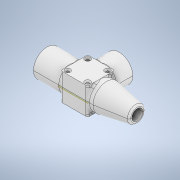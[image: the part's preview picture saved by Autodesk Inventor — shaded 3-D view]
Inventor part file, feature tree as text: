
AUTODESK INVENTOR PART (.ipt)
format: ipt  version: 2020 (Build 240168000, 168)  size: 861,696 bytes
history: native  units: mm
features: sketch x9, extrude x8, fillet x5, move_body x3, plane x2, chamfer x2, direct_edit x1, hole x1, split x1, projected_geometry x1
ambient origin geometry x8: Origin, YZ Plane, XZ Plane, XY Plane, X Axis, Y Axis, Z Axis, Center Point
bodies: Solid1 (feature_tree), Solid2 (feature_tree), Solid3 (feature_tree)
feature tree (33):
  extrude  "Extrusion1"  Depth=30.0mm
  extrude  "Extrusion2"  Depth=30.0mm
  extrude  "Extrusion3"  Depth=40.0mm TaperAngle=0.0deg
  extrude  "Extrusion4"  Depth=30.0mm TaperAngle=0.0deg
  direct_edit  "Direct Edit1"
  plane  "Work Plane1"
  extrude  "Extrusion6"  Depth=30.0mm
  fillet  "Fillet1"  Radius=20.0mm
  fillet  "Fillet2"  [1 undecoded]
  plane  "Work Plane2"
  extrude  "Extrusion7"  Depth=12.75mm
  fillet  "Fillet3"  Radius=12.8mm
  extrude  "Extrusion8"  Depth=4.0mm
  hole  "Hole1"  [1 undecoded]
  extrude  "Extrusion9"  [1 undecoded]
  fillet  "Fillet4"  Radius=20.4mm
  chamfer  "Chamfer1"  Distance=1.0mm
  fillet  "Fillet5"  Radius=0.5mm
  chamfer  "Chamfer2"  Distance=12.1mm
  split  "Split1"
  sketch  "Sketch1"  dims[d0=30.0mm d1=30.0mm]
  sketch  "Sketch2"  dims[d2=30.0mm d3=0.0mm d4=30.0mm]
  projected_geometry  "Projected Loop1"
  sketch  "Sketch3"  dims[d5=8.0mm d6=40.0mm d7=0.0mm]
  sketch  "Sketch4"  dims[d8=30.0mm d9=30.0mm d10=0.0mm]
  sketch  "Sketch6"  dims[d11=8.0mm d12=30.0mm d13=20.0mm d14=0.0mm]
  sketch  "Sketch7"  dims[d19=0.0mm d20=0.0mm d21=-14.5mm]
  sketch  "Sketch8"  dims[d22=0.0mm d23=0.0mm d24=-27.0mm]
  sketch  "Sketch9"  dims[d25=0.0mm d26=0.0mm d27=-15.0mm d28=-15.0mm]
  sketch  "Sketch10"  dims[d29=12.75mm d30=12.75mm d31=12.8mm d32=0.0mm d33=4.0mm d34=0.5mm d35=-30.0mm d36=20.4mm d37=1.0mm d38=0.0mm d39=0.5mm d40=12.1mm d41=25.0mm d42=0.0mm d43=22.0mm d44=22.0mm d45=3.0mm d46=6.0mm d47=6.0mm d48=2.0mm d49=90.0deg d50=8.0mm d51=20.594885mm d52=6.0mm d53=4.0mm d54=0.0mm d55=2.0mm d56=6.0mm d57=2.0mm d58=13.962634mm d59=2.0mm d60=6.0mm d61=2.0mm d62=13.962634mm]
  move_body  "Move1"
  move_body  "Move2"
  move_body  "Move3"
note: 3 required parameter values undecoded (feature->parameter linkage not recoverable at this tier; creation-order binding heuristic only, values carry confidence <= 0.55)
